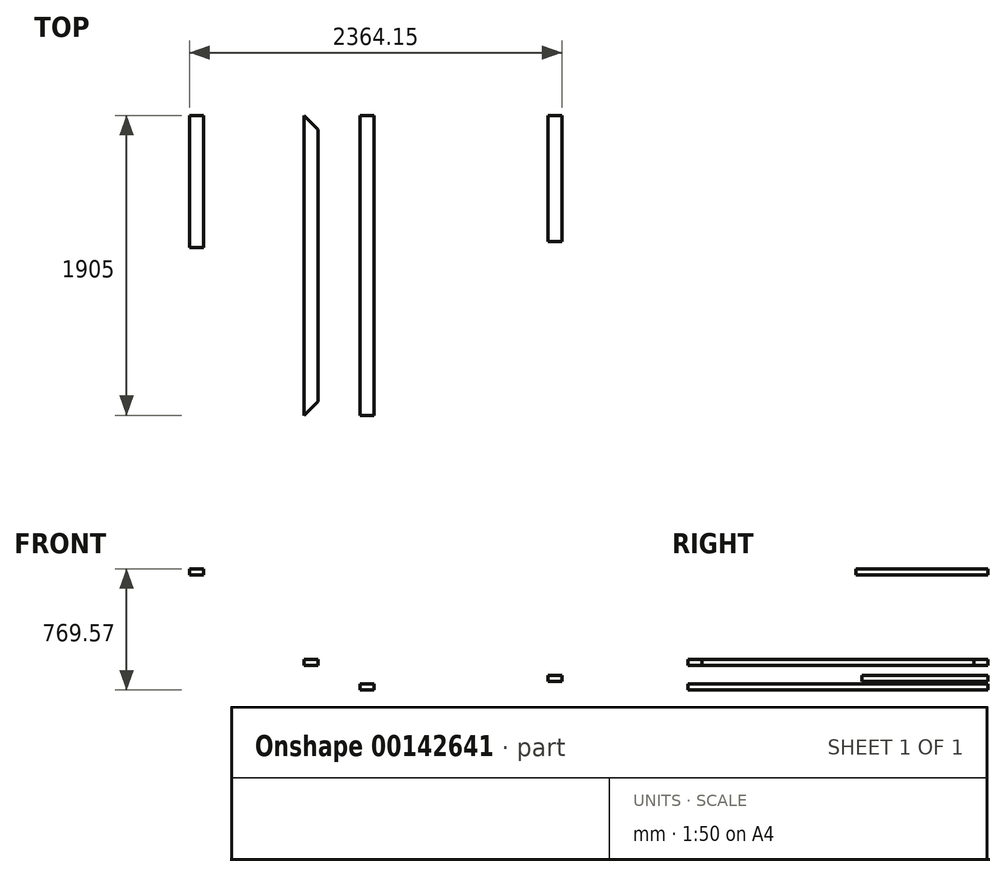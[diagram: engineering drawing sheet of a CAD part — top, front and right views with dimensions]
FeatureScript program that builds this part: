
annotation { "Feature Type Name" : "Feature", "Feature Type Description" : "" }
export const myFeature = defineFeature(function(context is Context, id is Id, definition is map)
    precondition{}
    {
        {
            var Q0;
            Q0=qCreatedBy(makeId("Front.planeOp"),FACE);
            var sketch = newSketch(context, id + "F0", { "sketchPlane" : qUnion([Q0])});
            skLineSegment(sketch, "E0.bottom", {"start": v(-65.46, 85.4) * mm, "end": v(23.44, 85.4) * mm});
            skLineSegment(sketch, "E0.top", {"start": v(-65.46, 47.3) * mm, "end": v(23.44, 47.3) * mm});
            skLineSegment(sketch, "E0.left", {"start": v(-65.46, 85.4) * mm, "end": v(-65.46, 47.3) * mm});
            skLineSegment(sketch, "E0.right", {"start": v(23.44, 85.4) * mm, "end": v(23.44, 47.3) * mm});
            skSolve(sketch);
        }
        {
            var Q0;
            Q0 = qSketchRegion(id + "F0", true);
            extrude(context, id + "F1", {"entities" : qUnion([Q0]), "depth" : 1905 * mm});
        }
        {
            var Q0;
            Q0=makeQuery(id+"F1.opExtrude","SWEPT_FACE",FACE,{"disambiguationData":[OSD([sQuery(id+"F0.wireOp",EDGE,"E0.bottom")])]});
            var sketch = newSketch(context, id + "F2", { "sketchPlane" : qUnion([Q0])});
            skLineSegment(sketch, "E1", {"start": v(-65.46, -1905) * mm, "end": v(23.44, -1816.1) * mm});
            skLineSegment(sketch, "E2", {"start": v(23.44, -1816.1) * mm, "end": v(23.44, -1905) * mm});
            skLineSegment(sketch, "E3", {"start": v(23.44, -1905) * mm, "end": v(-65.46, -1905) * mm});
            skLineSegment(sketch, "E4", {"start": v(23.44, -88.9) * mm, "end": v(-65.46, 0) * mm});
            skLineSegment(sketch, "E5", {"start": v(-65.46, 0) * mm, "end": v(23.44, 0) * mm});
            skLineSegment(sketch, "E6", {"start": v(23.44, 0) * mm, "end": v(23.44, -88.9) * mm});
            skSolve(sketch);
        }
        {
            var Q0;
            Q0 = qSketchRegion(id + "F2", true);
            extrude(context, id + "F3", {"entities" : qUnion([Q0]), "operationType" : NewBodyOperationType.REMOVE, "endBound" : BoundingType.UP_TO_NEXT, "oppositeDirection" : true, "depth" : 25.4 * mm});
        }
        {
            var Q0;
            Q0=qCreatedBy(makeId("Front.planeOp"),FACE);
            var sketch = newSketch(context, id + "F4", { "sketchPlane" : qUnion([Q0])});
            skLineSegment(sketch, "E7.bottom", {"start": v(292.64, -70.3) * mm, "end": v(381.54, -70.3) * mm});
            skLineSegment(sketch, "E7.top", {"start": v(292.64, -108.4) * mm, "end": v(381.54, -108.4) * mm});
            skLineSegment(sketch, "E7.left", {"start": v(292.64, -70.3) * mm, "end": v(292.64, -108.4) * mm});
            skLineSegment(sketch, "E7.right", {"start": v(381.54, -70.3) * mm, "end": v(381.54, -108.4) * mm});
            skSolve(sketch);
        }
        {
            var Q0;
            Q0 = qSketchRegion(id + "F4", true);
            extrude(context, id + "F5", {"entities" : qUnion([Q0]), "depth" : 1905 * mm});
        }
        {
            var Q0;
            Q0=qCreatedBy(makeId("Front.planeOp"),FACE);
            var sketch = newSketch(context, id + "F6", { "sketchPlane" : qUnion([Q0])});
            skLineSegment(sketch, "E8.bottom", {"start": v(1484.5, -16.33) * mm, "end": v(1573.4, -16.33) * mm});
            skLineSegment(sketch, "E8.top", {"start": v(1484.5, -54.43) * mm, "end": v(1573.4, -54.43) * mm});
            skLineSegment(sketch, "E8.left", {"start": v(1484.5, -16.33) * mm, "end": v(1484.5, -54.43) * mm});
            skLineSegment(sketch, "E8.right", {"start": v(1573.4, -16.33) * mm, "end": v(1573.4, -54.43) * mm});
            skSolve(sketch);
        }
        {
            var Q0;
            Q0 = qSketchRegion(id + "F6", true);
            extrude(context, id + "F7", {"entities" : qUnion([Q0]), "depth" : 800.1 * mm});
        }
        {
            var Q0;
            Q0=qCreatedBy(makeId("Front.planeOp"),FACE);
            var sketch = newSketch(context, id + "F8", { "sketchPlane" : qUnion([Q0])});
            skLineSegment(sketch, "E9.bottom", {"start": v(-790.75, 623.08) * mm, "end": v(-701.85, 623.08) * mm});
            skLineSegment(sketch, "E9.top", {"start": v(-790.75, 661.18) * mm, "end": v(-701.85, 661.18) * mm});
            skLineSegment(sketch, "E9.left", {"start": v(-790.75, 623.08) * mm, "end": v(-790.75, 661.18) * mm});
            skLineSegment(sketch, "E9.right", {"start": v(-701.85, 623.08) * mm, "end": v(-701.85, 661.18) * mm});
            skSolve(sketch);
        }
        {
            var Q0;
            Q0 = qSketchRegion(id + "F8", true);
            extrude(context, id + "F9", {"entities" : qUnion([Q0]), "depth" : 838.2 * mm});
        }
    });
